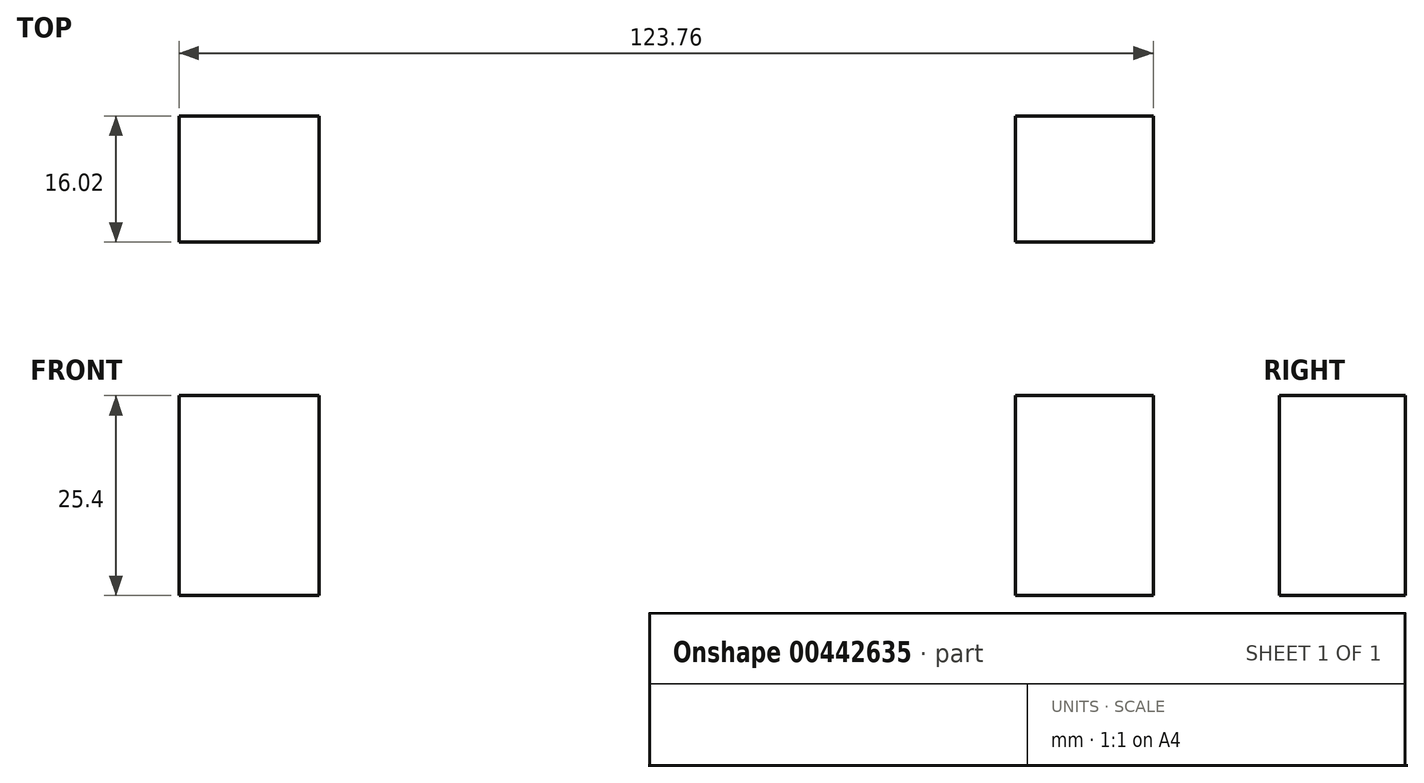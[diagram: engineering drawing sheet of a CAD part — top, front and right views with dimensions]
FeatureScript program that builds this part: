
annotation { "Feature Type Name" : "Feature", "Feature Type Description" : "" }
export const myFeature = defineFeature(function(context is Context, id is Id, definition is map)
    precondition{}
    {
        {
            var Q0;
            Q0=qCreatedBy(makeId("Top.planeOp"),FACE);
            var sketch = newSketch(context, id + "F0", { "sketchPlane" : qUnion([Q0])});
            skLineSegment(sketch, "E0.bottom", {"start": v(-69.63, 0) * mm, "end": v(-51.85, 0) * mm});
            skLineSegment(sketch, "E0.top", {"start": v(-69.63, 16.02) * mm, "end": v(-51.85, 16.02) * mm});
            skLineSegment(sketch, "E0.left", {"start": v(-69.63, 0) * mm, "end": v(-69.63, 16.02) * mm});
            skLineSegment(sketch, "E0.right", {"start": v(-51.85, 0) * mm, "end": v(-51.85, 16.02) * mm});
            skLineSegment(sketch, "E1.bottom", {"start": v(36.63, 16.02) * mm, "end": v(54.13, 16.02) * mm});
            skLineSegment(sketch, "E1.top", {"start": v(36.63, 0) * mm, "end": v(54.13, 0) * mm});
            skLineSegment(sketch, "E1.left", {"start": v(36.63, 16.02) * mm, "end": v(36.63, 0) * mm});
            skLineSegment(sketch, "E1.right", {"start": v(54.13, 16.02) * mm, "end": v(54.13, 0) * mm});
            skSolve(sketch);
        }
        {
            var Q0;
            Q0 = qSketchRegion(id + "F0", true);
            extrude(context, id + "F1", {"entities" : qUnion([Q0]), "depth" : 25.4 * mm});
        }
    });
